# Revit family: IS_Contour21_S4093_BIM_DE
name_source: partatom
category: Plumbing Fixtures
revit_build: Autodesk Revit MEP 2016 (Build: 20161004_0715(x64)
units: mm (PartAtom-declared; Revit-internal decimal feet)

## family parameters
Always vertical = No
Cut with Voids When Loaded = No
OmniClass Number = 23.45.05.21.11.11
OmniClass Title = Water Operated Water Closets
Part Type = Normal
Room Calculation Point = No
Round Connector Dimension = Use Diameter
Shared = No
Work Plane-Based = No

## types (1)
- S409301 - CONTOUR21 seat & cover for children
    Accessories = www.idealstandard.de\ersatzteile
    AssetType = Fixed
    BIMObjectName = ISI_IdealStandard_WcSeatsAndCovers_Contour21_S409301
    BIMobject category = Toilet Seats
    BOSUseNativeGeometries = 1
    BarCode = 5017830410379
    Brand = Ideal Standard
    Brand url = http://www.idealstandard.de
    CodePerformance = 0
    Color = White
    ConnectionType = Plumbing
    Cost = 0 $
    CurrencyUnit = €
    CurrentRevision = 1
    Date of publishing = 20/12/2017
    Description = IS Kinder-WC-Sitz CONTOUR 21 Weiß
    DurationUnit = Year
    EAN code = https://5017830410379
    Edition number = 1
    ExpectedLife = 25
    Features = IS Kinder-WC-Sitz CONTOUR 21 Weiß
    Finish = White
    IFC Classification = Sanitary Terminal
    IfcExportAs = IfcSanitaryTerminalType
    Installation instructions = http://www.idealstandard.de
    InstallationInstructions = www.idealstandard.de\produkte
    MainColor = White
    MaintenanceInformation = www.idealstandard.de\produkte
    Manufacturer name = Ideal Standard
    ManufacturerURL = http://www.idealstandard.de
    Material = Duroplast
    Model = S409301
    ModelNumber = S409301
    ModelReference = IS Kinder-WC-Sitz CONTOUR 21 Weiß
    Name = WcSeatsAndCovers_Contour21_S409301
    NettWeight = 2.7 Kg
    Nominal height = 68
    Nominal width = 375
    NominalDepth = 438 mm  [stored 1.43701 ft]
    NominalHeight = 66 mm
    NominalLength = 438 mm  [stored 1.43701 ft]
    NominalWidth = 375 mm  [stored 1.23031 ft]
    OutletConnectionSize = 0 mm  [stored 0 ft]
    Product Guid = 5b51143a-1681-4f03-96b9-5b0a70a4b1df
    Product SKU = S4093
    Product data url = https://bimobject.com
    Product family = Sanitary
    Product group = Seat & Cover
    Product name = CONTOUR21 seat & cover for children
    Product url = http://www.idealstandard.de
    ProductInformation = www.idealstandard.de/produkte
    QR code = http://bimobject.com
    Shape = Sculptured
    Size = 66 x 439 x 375mm
    Space = Internal
    SpareParts = www.idealstandard.de/ersatzteile
    SpilloverLevel = 0 mm  [stored 0 ft]
    Technical description = http://www.idealstandard.de
    URL = http://www.idealstandard.de
    Uniclass2015Code = Pr_40_20_93_95
    Uniclass2015Title = WC seats and covers
    Uniclass2015Version = Products v1.1
    Version = 1
    VolumeUnits = Litres
    Weight Net (Kg) = 2.7

note: [stored X ft] marks values corroborated as IEEE doubles in the binary element streams (Revit-internal decimal feet)

## geometry (parser evidence)
native form markers: Blend x4, Sweep x1
no freeform markers — native parametric forms only
